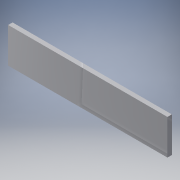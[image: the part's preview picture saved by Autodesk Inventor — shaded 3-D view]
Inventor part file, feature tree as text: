
AUTODESK INVENTOR PART (.ipt)
format: ipt  version: 2016 (Build 200138000, 138)  size: 88,576 bytes
history: native  units: in
note: dims shown in document units (in); Inventor stores cm internally (conversion verified against a paired STEP export)
features: extrude x1, sketch x1
ambient origin geometry x8: Origin, YZ Plane, XZ Plane, XY Plane, X Axis, Y Axis, Z Axis, Center Point
bodies: Solid1 (feature_tree)
feature tree (2):
  extrude  "Extrusion1"  Depth=4.525in
  sketch  "Sketch1"  dims[d0=1.0in d1=4.525in d2=0.125in d3=0.0in]
